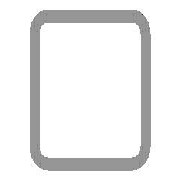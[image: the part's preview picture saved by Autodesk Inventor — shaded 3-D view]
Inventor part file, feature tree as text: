
AUTODESK INVENTOR PART (.ipt)
format: ipt  version: 2024 (Build 280153000, 153)  size: 157,696 bytes
history: native  units: mm (DEFAULTED — no unit token found)
features: other x4, plane x4, split x3, extrude x1, sketch x1
ambient origin geometry x8: Origin, YZ Plane, XZ Plane, XY Plane, X Axis, Y Axis, Z Axis, Center Point
bodies: Solid1 (feature_tree)
feature tree (13):
  parser-record x1  (decoder bookkeeping rows leaked as tree rows — omitted from the tree; the rows remain in map.json)
  other  "Driven Length"
  other  "Plano inicial"
  other  "Plano final"
  extrude  "Cuerpo"  TaperAngle=0.0deg  [1 undecoded]
  plane  "Plano de trabajo4"
  split  "Dividir1"
  plane  "Plano de trabajo5"
  split  "Dividir2"
  plane  "Plano de trabajo6"
  split  "Dividir3"
  sketch  "Sketch3"  dims[d3=1173.540128mm d4=0.0mm d10=50.8mm d11=50.8mm d12=3.175mm d13=-25.4mm d14=1148.140128mm d15=25.4mm d16=25.4mm d17=6.35mm d18=90.0deg d19=1173.540128mm]
  plane  "Work Plane3"
note: 1 required parameter value undecoded (feature->parameter linkage not recoverable at this tier; creation-order binding heuristic only, values carry confidence <= 0.55)
